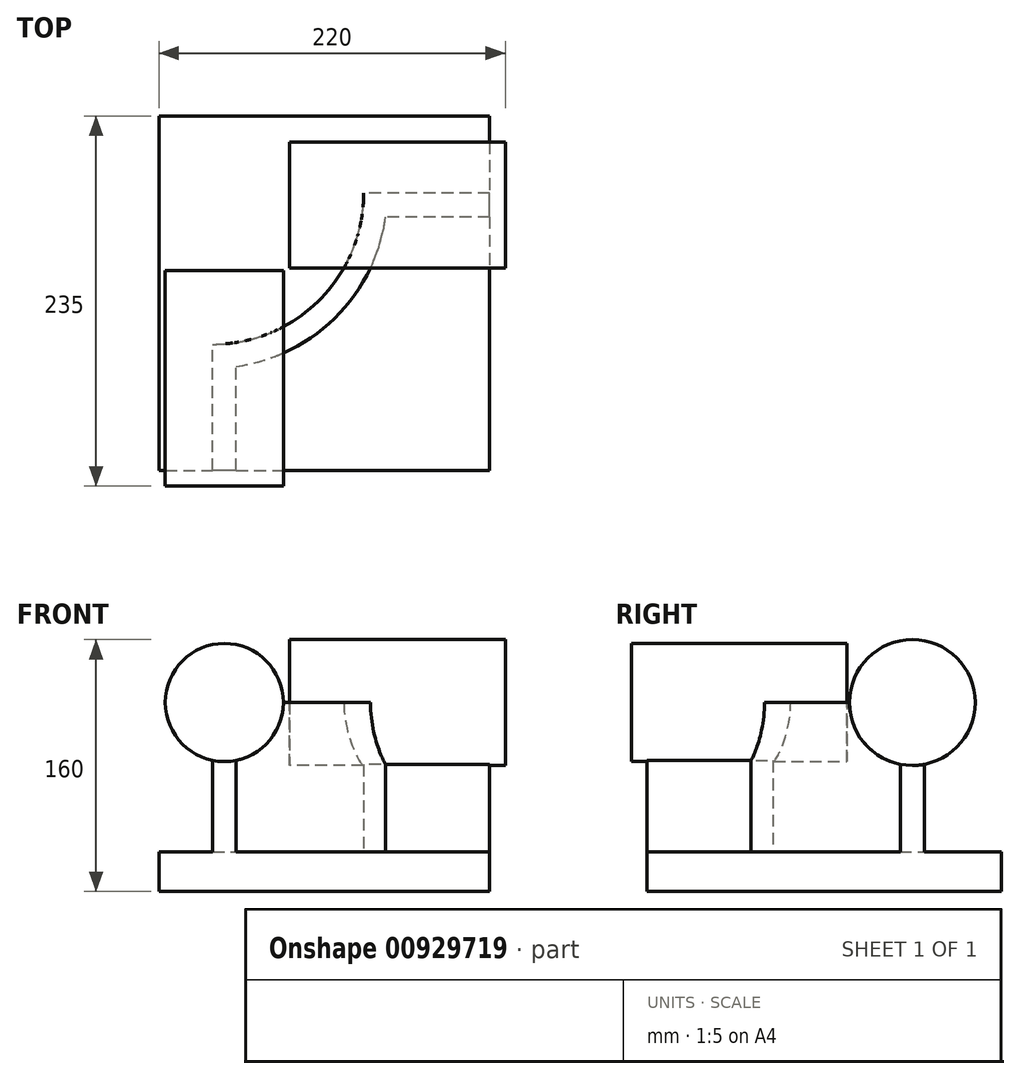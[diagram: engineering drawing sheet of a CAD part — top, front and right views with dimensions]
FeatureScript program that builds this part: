
annotation { "Feature Type Name" : "Feature", "Feature Type Description" : "" }
export const myFeature = defineFeature(function(context is Context, id is Id, definition is map)
    precondition{}
    {
        {
            var Q0;
            Q0=qCreatedBy(makeId("Top.planeOp"),FACE);
            var sketch = newSketch(context, id + "F0", { "sketchPlane" : qUnion([Q0])});
            skLineSegment(sketch, "E0.bottom", {"start": v(-105, 112.5) * mm, "end": v(105, 112.5) * mm});
            skLineSegment(sketch, "E0.top", {"start": v(-105, -112.5) * mm, "end": v(105, -112.5) * mm});
            skLineSegment(sketch, "E0.left", {"start": v(-105, 112.5) * mm, "end": v(-105, -112.5) * mm});
            skLineSegment(sketch, "E0.right", {"start": v(105, 112.5) * mm, "end": v(105, -112.5) * mm});
            skPoint(sketch, "E0.middle", {"position": v(0, 0) * mm});
            skSolve(sketch);
        }
        {
            var Q0;
            Q0=makeQuery(id+"F0.imprint","IMPRINT",FACE,{"disambiguationData":[TD([[makeQuery(id+"F0.imprint","IMPRINT",EDGE,{"derivedFrom":sQuery(id+"F0.wireOp",EDGE,"E0.bottom")}),-1.0]])]});
            extrude(context, id + "F1", {"entities" : qUnion([Q0]), "depth" : 25 * mm, "offsetDistance" : 25 * mm});
        }
        {
            var Q0;
            Q0=makeQuery(id+"F1.opExtrude","CAP_FACE",FACE,{"disambiguationData":[OSD([sQuery(id+"F0.wireOp",EDGE,"E0.bottom"),sQuery(id+"F0.wireOp",EDGE,"E0.top"),sQuery(id+"F0.wireOp",EDGE,"E0.left"),sQuery(id+"F0.wireOp",EDGE,"E0.right")])],"isStart":false});
            var sketch = newSketch(context, id + "F2", { "sketchPlane" : qUnion([Q0])});
            skLineSegment(sketch, "E1", {"start": v(-71, -112.5) * mm, "end": v(-71, -32.5) * mm});
            skLineSegment(sketch, "E2", {"start": v(105, 63.5) * mm, "end": v(25, 63.5) * mm});
            skArc(sketch, "E3", {"start": v(-71, -32.5) * mm, "mid": v(-3.12, -4.38) * mm, "end": v(25, 63.5) * mm});
            skLineSegment(sketch, "E4", {"start": v(-71, 63.5) * mm, "end": v(25, 63.5) * mm, "construction": true});
            skLineSegment(sketch, "E5", {"start": v(-71, 63.5) * mm, "end": v(-71, -32.5) * mm, "construction": true});
            skLineSegment(sketch, "E6.0", {"start": v(-56, -112.5) * mm, "end": v(-56, -46.48) * mm});
            skArc(sketch, "E6.1", {"start": v(-56, -46.48) * mm, "mid": v(7.49, -14.99) * mm, "end": v(38.98, 48.5) * mm});
            skLineSegment(sketch, "E6.2", {"start": v(105, 48.5) * mm, "end": v(38.98, 48.5) * mm});
            skLineSegment(sketch, "E7.0", {"start": v(105, 112.5) * mm, "end": v(105, -112.5) * mm});
            skLineSegment(sketch, "E8.0", {"start": v(-105, -112.5) * mm, "end": v(105, -112.5) * mm});
            skSolve(sketch);
        }
        {
            var Q0;
            {var subQ2=sQuery(id+"F2.wireOp",EDGE,"E1");Q0=makeQuery(id+"F2.imprint","IMPRINT",FACE,{"disambiguationData":[TD([[makeQuery(id+"F2.imprint","IMPRINT",EDGE,{"derivedFrom":subQ2}),-1.0]])]});}
            extrude(context, id + "F3", {"entities" : qUnion([Q0]), "operationType" : NewBodyOperationType.ADD, "depth" : 95 * mm, "offsetDistance" : 25 * mm});
        }
        {
            var Q0;
            Q0=makeQuery(id+"F3.boolean.opBoolean","MERGE",FACE,{"derivedFrom":[makeQuery(id+"F1.opExtrude","SWEPT_FACE",FACE,{"disambiguationData":[OSD([sQuery(id+"F0.wireOp",EDGE,"E0.right")])]}),makeQuery(id+"F3.opExtrude","SWEPT_FACE",FACE,{"disambiguationData":[OSD([sQuery(id+"F2.wireOp",EDGE,"E7.0")])]})]});
            var sketch = newSketch(context, id + "F4", { "sketchPlane" : qUnion([Q0])});
            skCircle(sketch, "E9", {"center": v(56, 120) * mm, "radius": 40 * mm});
            skSolve(sketch);
        }
        {
            var Q0;
            Q0 = qSketchRegion(id + "F4", true);
            extrude(context, id + "F5", {"entities" : qUnion([Q0]), "operationType" : NewBodyOperationType.ADD, "depth" : 10 * mm, "offsetDistance" : 25 * mm, "hasSecondDirection" : true, "secondDirectionOppositeDirection" : true, "secondDirectionDepth" : (137 - 10) * mm});
        }
        {
            var Q0;
            Q0=makeQuery(id+"F3.boolean.opBoolean","MERGE",FACE,{"derivedFrom":[makeQuery(id+"F1.opExtrude","SWEPT_FACE",FACE,{"disambiguationData":[OSD([sQuery(id+"F0.wireOp",EDGE,"E0.top")])]}),makeQuery(id+"F3.opExtrude","SWEPT_FACE",FACE,{"disambiguationData":[OSD([sQuery(id+"F2.wireOp",EDGE,"E8.0")])]})]});
            var sketch = newSketch(context, id + "F6", { "sketchPlane" : qUnion([Q0])});
            skCircle(sketch, "E10", {"center": v(-63.5, 120) * mm, "radius": 37.5 * mm});
            skSolve(sketch);
        }
        {
            var Q0;
            Q0 = qSketchRegion(id + "F6", true);
            var Q1;
            {var subQ1=sQuery(id+"F2.wireOp",EDGE,"E8.0");var subQ6=makeQuery(id+"F3.opExtrude","CAP_EDGE",EDGE,{"disambiguationData":[OSD([subQ1])],"isStart":false});Q1=makeQuery(id+"F6.imprint","IMPRINT",FACE,{"disambiguationData":[TD([[makeQuery(id+"F6.imprint","IMPRINT",EDGE,{"derivedFrom":subQ6}),1.0]])]});}
            extrude(context, id + "F7", {"entities" : qUnion([Q0, Q1]), "operationType" : NewBodyOperationType.ADD, "depth" : 10 * mm, "offsetDistance" : 25 * mm, "hasSecondDirection" : true, "secondDirectionOppositeDirection" : true, "secondDirectionDepth" : (137 - 10) * mm});
        }
    });
